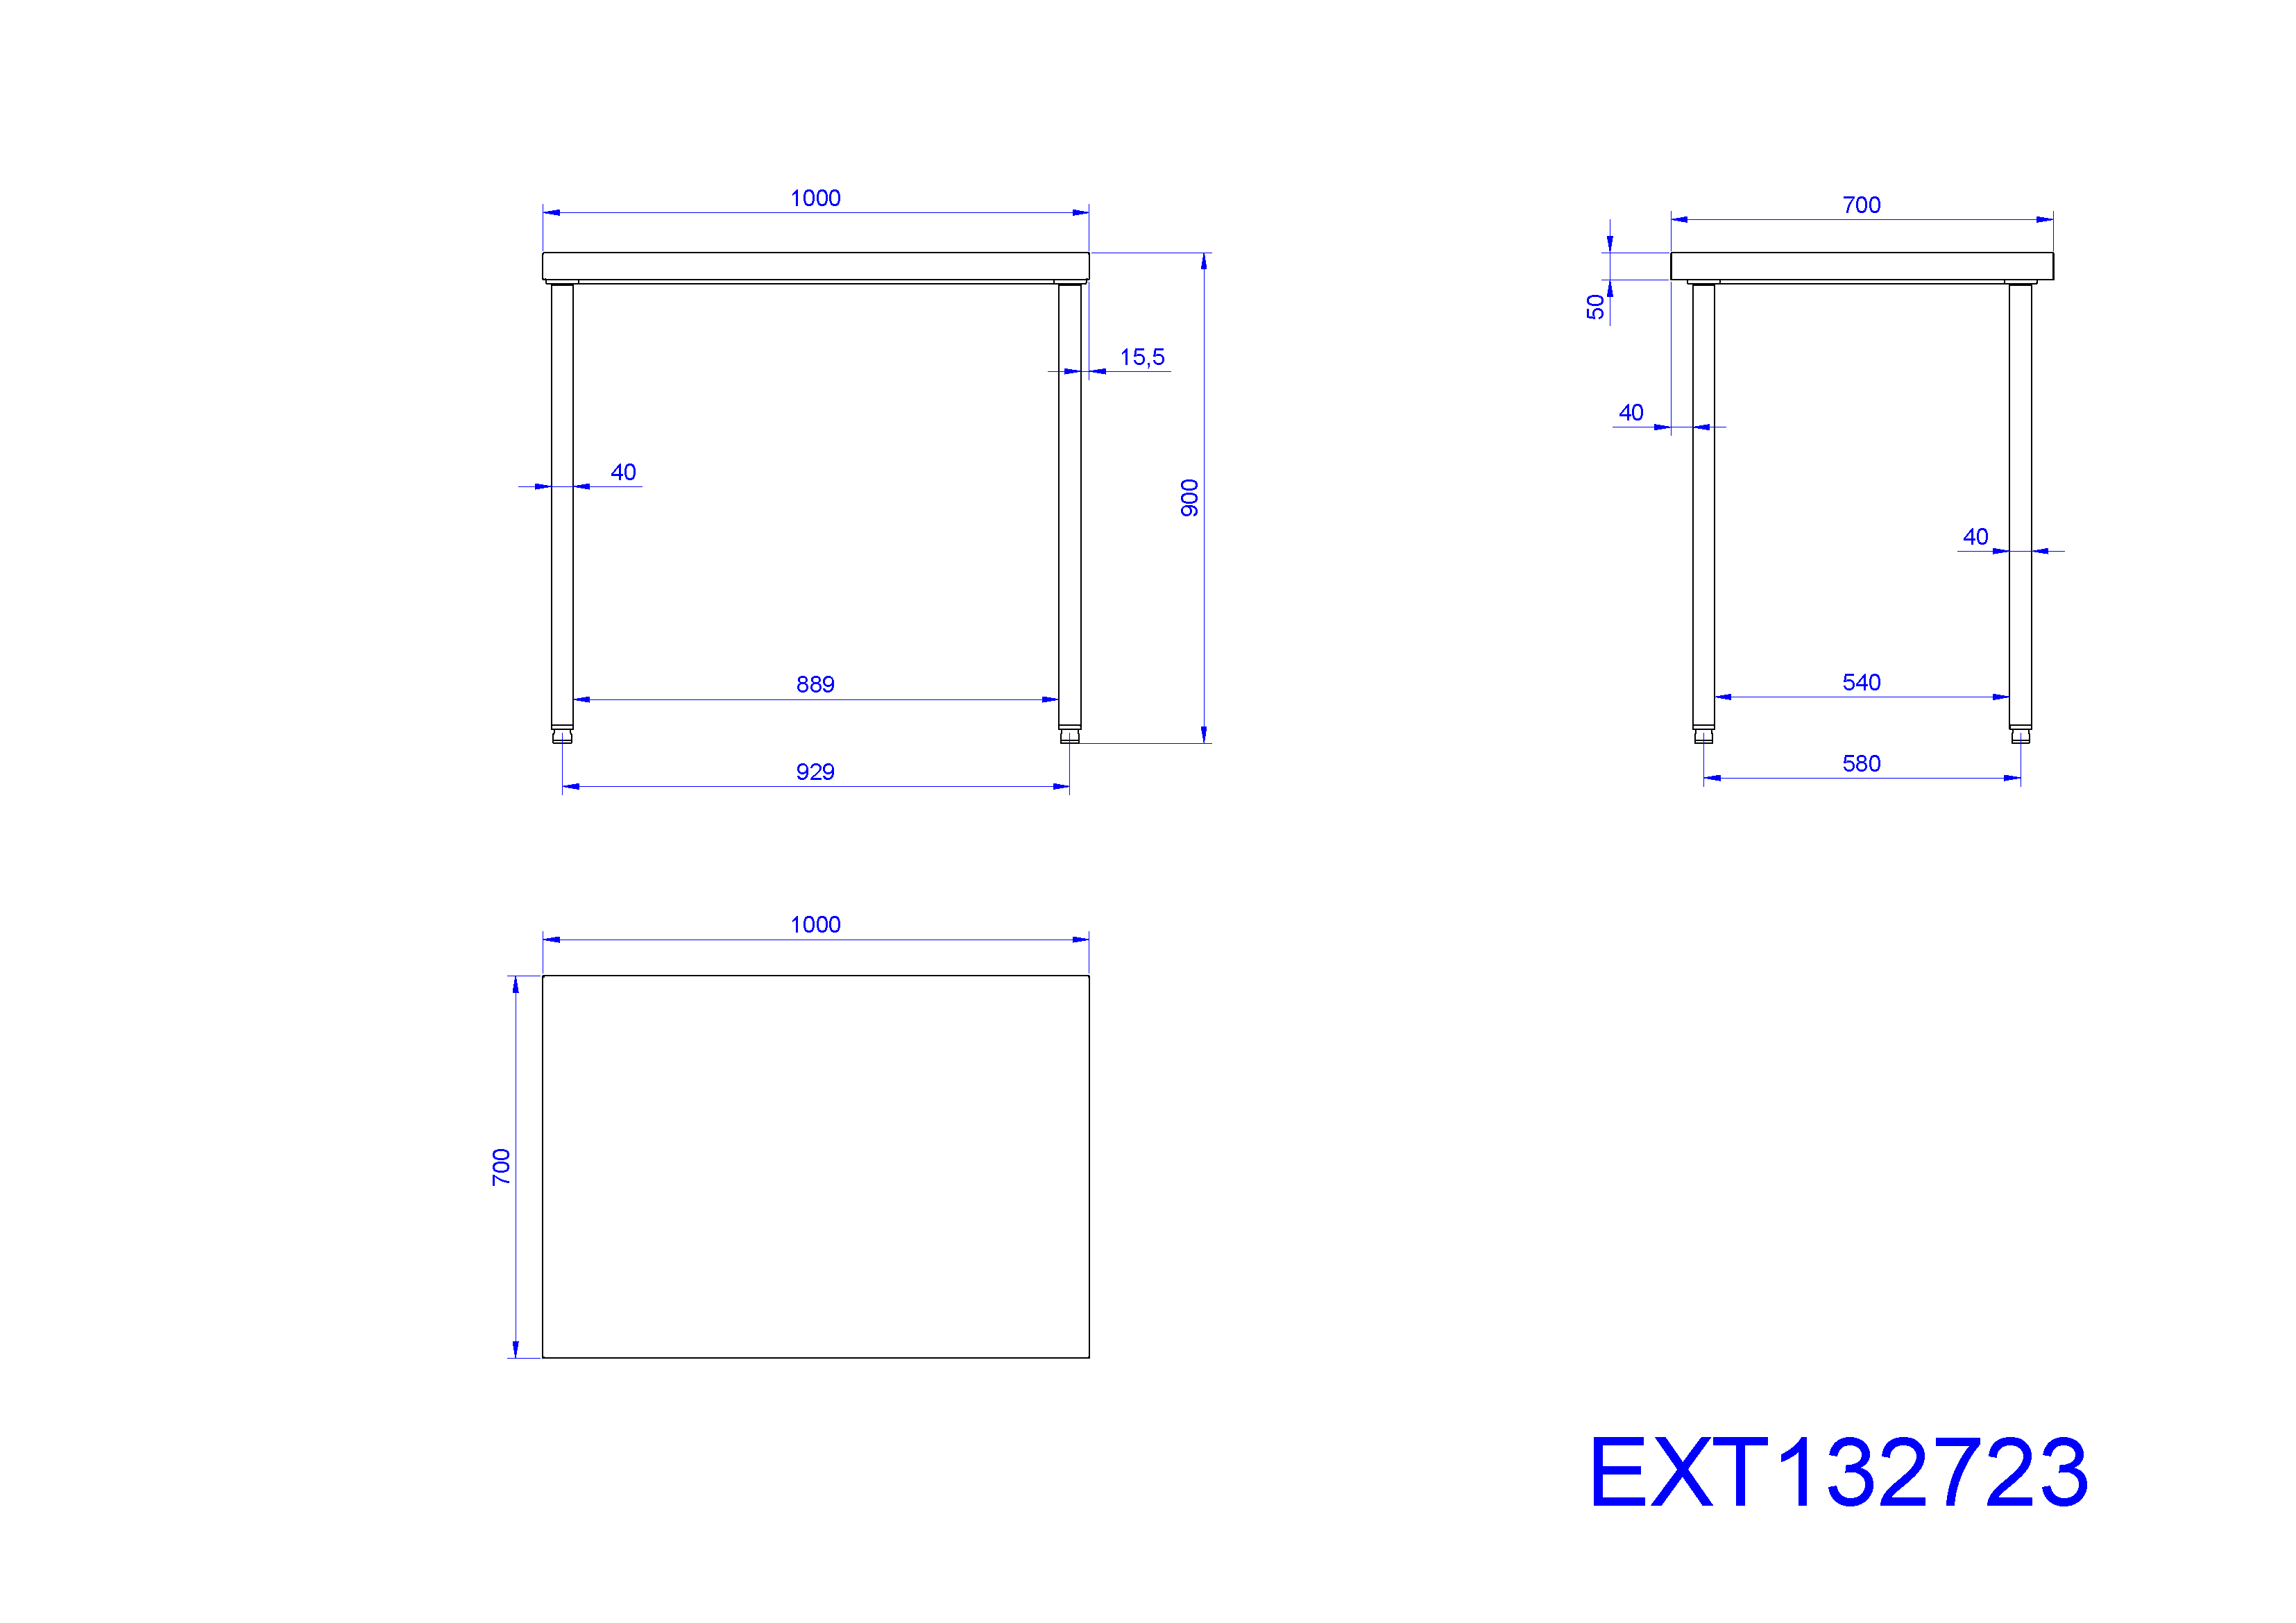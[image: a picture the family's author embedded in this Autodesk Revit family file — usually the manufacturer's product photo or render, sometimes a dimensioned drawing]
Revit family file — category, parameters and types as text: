
# Revit family: QF_ELECTROLUXPROFESSIONAL_134137_GLG1225P
name_source: partatom
category: Attrezzature speciali
units: mm (PartAtom-declared; Revit-internal decimal feet)

## family parameters
Basato su piano di lavoro = No
Condiviso = No
Punto di calcolo locali = No
Quota connettore circolare = Usa diametro
Sempre verticale = Sì
Taglio con vuoti quando caricato = No
Tipo di parte = Normale

## types (1)
- Standard
    Accessory = Sì
    Cold Water Size = 0 mm
    Compressed Air Pressure = 0.0 Pa
    Compressed Air Size = 0 mm
    Compressed Air Volume = 0.0 L/s
    Condensate Return Size = 0 mm
    Cycle = 0 Hz
    Depth Actual = 700 mm  [stored 2.29659 ft]
    Descrizione = SINK CUPBOARD 2 BOWLS 1200 MM
    Direct Waste Size = 0 mm
    Gas Input Pressure = 0
    Gas KW = 0
    Gas Size = 0 mm
    HP = 0 HP
    Height Actual = 1000 mm  [stored 3.28084 ft]
    Hot Water Size = 0 mm
    Item Number = 134137
    Length Actual = 1200 mm
    Modello = GLG1225P
    Phase = 0
    Produttore = Electrolux Professional
    Prospetto di default = 0 mm  [stored 0 ft]
    Refrigerant Compressor Remote = Sì
    Refrigeration Liquid Line Size = 0 mm  [stored 0 ft]
    Refrigeration Suction Line Size = 0 mm  [stored 0 ft]
    Steam Consumption per Hour = 0
    Steam Supply Maximum Pressure = 0.0 Pa
    Steam Supply Minimum Pressure = 0.0 Pa
    Steam Supply Size = 0 mm
    URL = https://www.electroluxprofessional.com
    URL Manufacturer = https://www.electroluxprofessional.com
    Volts = 0 V
    Watts = 0 W
    Weight = 54.00 kg

note: source unit labels omitted for Gas Input Pressure — the stored unit's dimension contradicts the parameter name (converter mislabeling)

note: [stored X ft] marks values corroborated as IEEE doubles in the binary element streams (Revit-internal decimal feet)

## geometry (parser evidence)
native form markers: Sweep x5
no freeform markers — native parametric forms only
